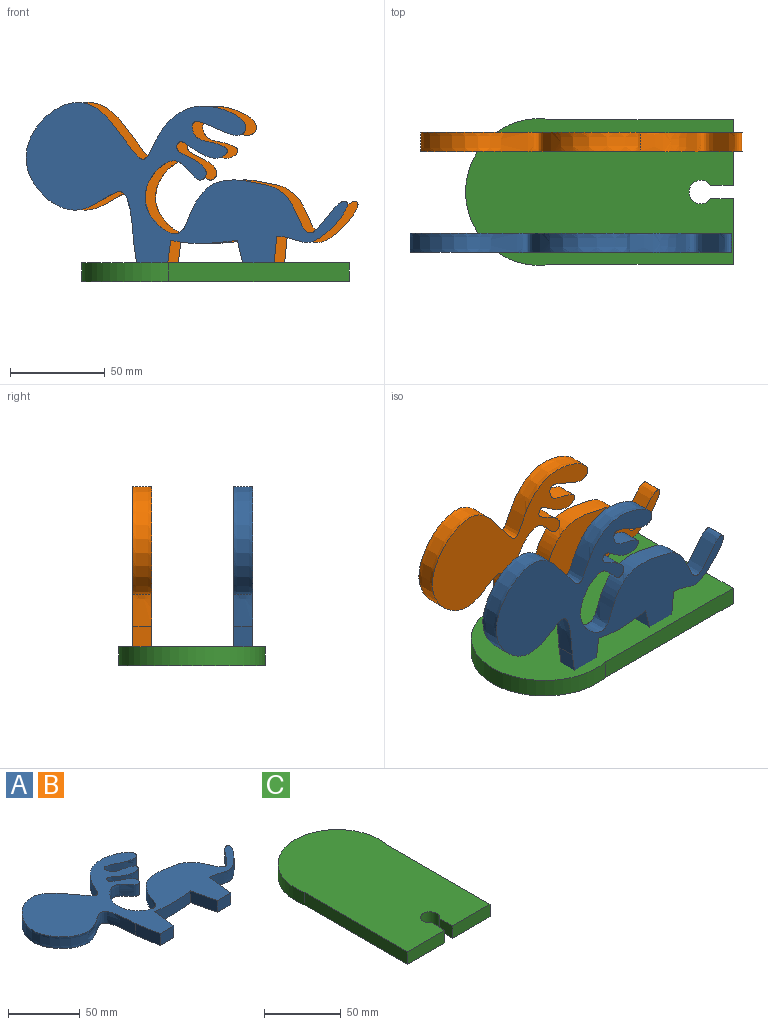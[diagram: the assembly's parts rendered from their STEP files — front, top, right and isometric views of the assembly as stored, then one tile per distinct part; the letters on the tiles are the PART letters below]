
ASSEMBLY  parts=3 mates=4
PART A: 10 faces, bbox 173.5x96.3x10 mm
  f0: plane 20.68x10mm, normal (-0.99,-0.15,0), area 209.1mm2, adj f1,f7,f8,f9
  f1: plane 13.6x10mm, normal (0,-1,0), area 136mm2, adj f0,f2,f8,f9
  f2: plane 21.81x10mm, normal (0.99,-0.13,0), area 220mm2, adj f1,f3,f8,f9
  f3: extruded ~35.13x10mm, area 353.7mm2, adj f2,f4,f8,f9
  f4: plane 21.81x10mm, normal (-0.97,-0.23,0), area 224mm2, adj f3,f5,f8,f9
  f5: plane 13.31x10mm, normal (0,-1,0), area 133.1mm2, adj f4,f6,f8,f9
  f6: plane 23.95x10mm, normal (1,-0.1,0), area 240.7mm2, adj f5,f7,f8,f9
  f7: extruded ~163.01x73.72mm, area 6228mm2, adj f0,f6,f8,f9
  f8: plane 173.52x96.28mm, normal (0,0,1), area 6205.9mm2, adj f0,f1,f2,f3,f4,f5,f6,f7
  f9: plane 173.52x96.28mm, normal (0,0,-1), area 6205.9mm2, adj f0,f1,f2,f3,f4,f5,f6,f7
PART B: same geometry as A
PART C: 10 faces, bbox 77.4x141.1x10 mm
  f0: plane 34.49x10mm, normal (0,-1,0), area 344.9mm2, adj f1,f2,f5,f9
  f1: plane 141.11x77.36mm, normal (0,0,1), area 9938.5mm2, adj f0,f3,f4,f5,f6,f7,f8,f9
  f2: plane 141.11x77.36mm, normal (0,0,-1), area 9938.5mm2, adj f0,f3,f4,f5,f6,f7,f8,f9
  f3: plane 95.18x10mm, normal (-1,0,0), area 951.8mm2, adj f1,f2,f4,f6
  f4: plane 34.49x10mm, normal (0,-1,0), area 344.9mm2, adj f1,f2,f3,f8
  f5: plane 95.18x10mm, normal (1,0,0), area 951.8mm2, adj f0,f1,f2,f6
  f6: cylinder r=38.68mm len=77.36mm, axis (0,0,-1), area 1360.9mm2, adj f1,f2,f3,f5
  f7: cylinder r=6.25mm len=12.5mm, axis (0,0,1), area 318.5mm2, adj f1,f2,f8,f9
  f8: plane 11.9x10mm, normal (1,0,0), area 119mm2, adj f1,f2,f4,f7
  f9: plane 11.96x10mm, normal (-1,0,0), area 119.6mm2, adj f0,f1,f2,f7
PLACE A rot(axis=(1,0,0),90deg) t=(76.3,-133.18,78.61)mm
PLACE B rot(axis=(1,0,0),90deg) t=(81.83,-80.01,78.61)mm
PLACE C rot(axis=(0,0,1),90deg) t=(84.53,-95.99,27.48)mm
MATE planar A.f5 <-> C.f1  axis (0,0,-1) through (93.3,-138.18,27.48)mm
MATE planar C.f2 <-> A.f1  axis (0,0,-1) through (72.56,-111.26,27.48)mm
MATE planar B.f1 <-> C.f2  axis (0,0,-1) through (42.31,-85.01,27.48)mm
MATE parallel C.f2 <-> B.f5  axis (0,0,-1) through (72.56,-111.26,27.48)mm
